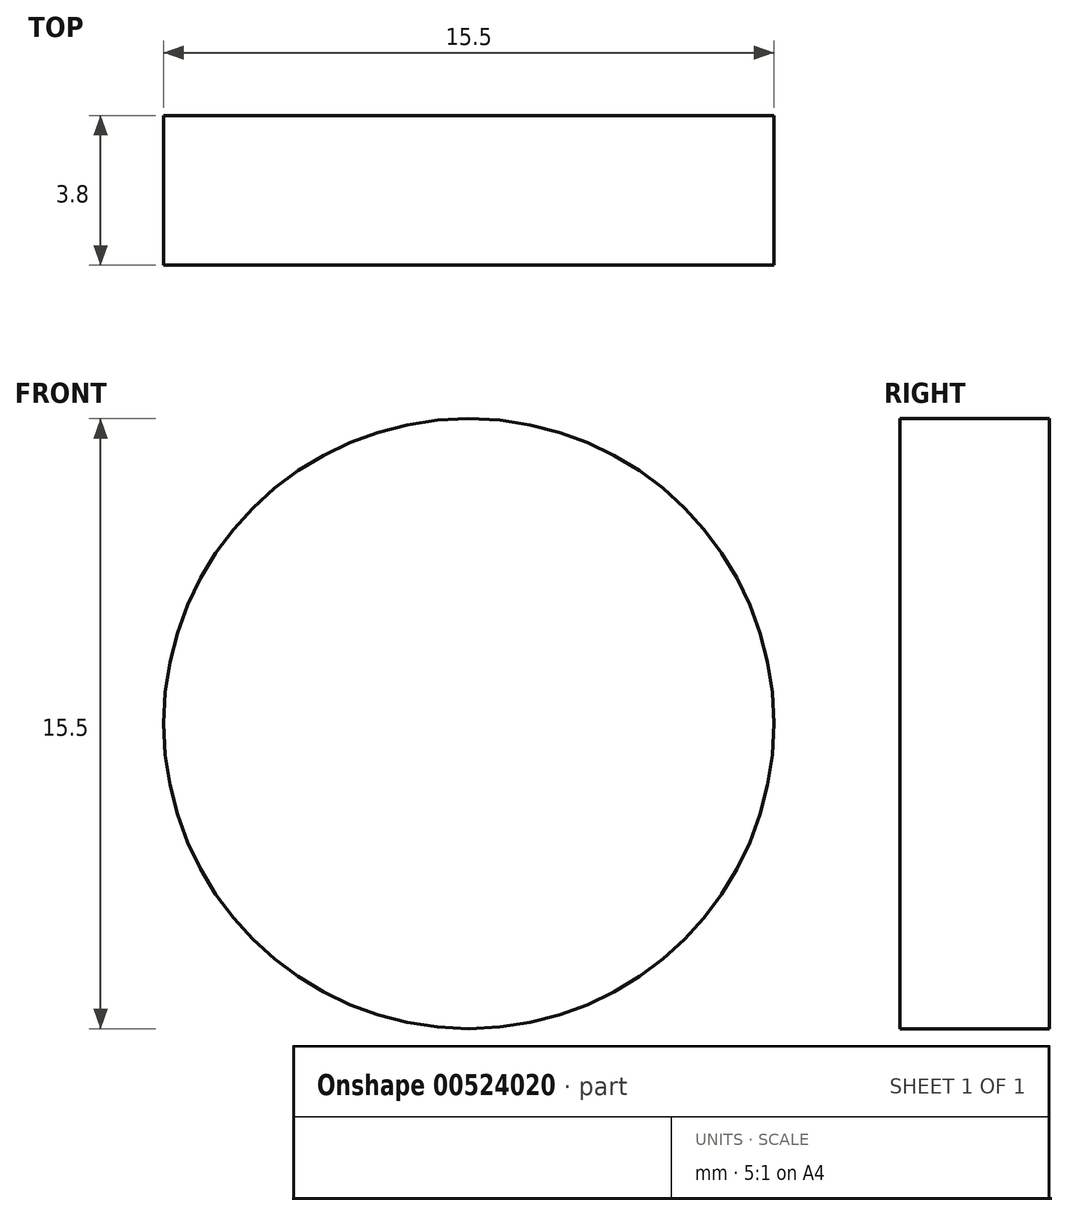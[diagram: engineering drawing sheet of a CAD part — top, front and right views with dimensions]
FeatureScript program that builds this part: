
annotation { "Feature Type Name" : "Feature", "Feature Type Description" : "" }
export const myFeature = defineFeature(function(context is Context, id is Id, definition is map)
    precondition{}
    {
        {
            var Q0;
            Q0=qCreatedBy(makeId("Front.planeOp"),FACE);
            var sketch = newSketch(context, id + "F0", { "sketchPlane" : qUnion([Q0])});
            skCircle(sketch, "E0", {"center": v(0, 0) * mm, "radius": 7.75 * mm});
            skSolve(sketch);
        }
        {
            var Q0;
            Q0=makeQuery(id+"F0.imprint","IMPRINT",FACE,{"disambiguationData":[TD([[makeQuery(id+"F0.imprint","IMPRINT",EDGE,{"derivedFrom":sQuery(id+"F0.wireOp",EDGE,"E0")}),1.0]])]});
            extrude(context, id + "F1", {"entities" : qUnion([Q0]), "depth" : 3.8 * mm, "offsetDistance" : 25 * mm});
        }
    });
